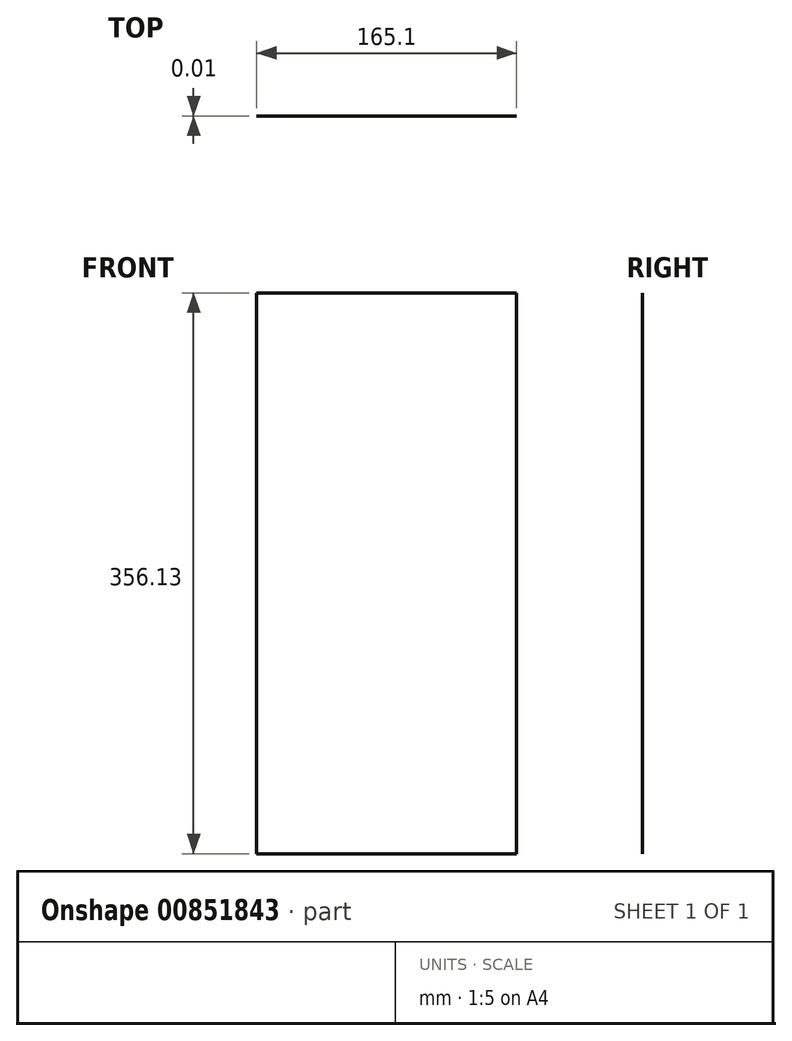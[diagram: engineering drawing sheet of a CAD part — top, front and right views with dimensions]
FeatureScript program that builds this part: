
annotation { "Feature Type Name" : "Feature", "Feature Type Description" : "" }
export const myFeature = defineFeature(function(context is Context, id is Id, definition is map)
    precondition{}
    {
        {
            var Q0;
            Q0=qCreatedBy(makeId("Front.planeOp"),FACE);
            var sketch = newSketch(context, id + "F0", { "sketchPlane" : qUnion([Q0])});
            skLineSegment(sketch, "E0.bottom", {"start": v(-96.95, 163.97) * mm, "end": v(68.15, 163.97) * mm});
            skLineSegment(sketch, "E0.top", {"start": v(-96.95, -192.16) * mm, "end": v(68.15, -192.16) * mm});
            skLineSegment(sketch, "E0.left", {"start": v(-96.95, 163.97) * mm, "end": v(-96.95, -192.16) * mm});
            skLineSegment(sketch, "E0.right", {"start": v(68.15, 163.97) * mm, "end": v(68.15, -192.16) * mm});
            skSolve(sketch);
        }
        {
            var Q0;
            Q0=makeQuery(id+"F0.imprint","IMPRINT",FACE,{"disambiguationData":[TD([[makeQuery(id+"F0.imprint","IMPRINT",EDGE,{"derivedFrom":sQuery(id+"F0.wireOp",EDGE,"E0.bottom")}),-1.0]])]});
            var Q1;
            Q1 = qSketchRegion(id + "F0", true);
            extrude(context, id + "F1", {"entities" : qUnion([Q0, Q1]), "depth" : 1 / 101.6 * mm, "offsetDistance" : 25.4 * mm});
        }
        {
            var Q0;
            Q0=makeQuery(id+"F1.opExtrude","SWEPT_FACE",FACE,{"disambiguationData":[OSD([sQuery(id+"F0.wireOp",EDGE,"E0.bottom")])]});
            var sketch = newSketch(context, id + "F2", { "sketchPlane" : qUnion([Q0])});
            skLineSegment(sketch, "E1", {"start": v(-14.4, -6.35) * mm, "end": v(-14.4, 0) * mm});
            skPoint(sketch, "E2", {"position": v(-14.4, -3.18) * mm});
            skSolve(sketch);
        }
        {
            var Q0;
            Q0=sQuery(id+"F2.wireOp",VERTEX,"E2");
            var Q1;
            Q1=makeQuery(id+"F1.opExtrude","SWEPT_BODY",BODY,{"disambiguationData":[OSD([sQuery(id+"F0.wireOp",EDGE,"E0.bottom"),sQuery(id+"F0.wireOp",EDGE,"E0.top"),sQuery(id+"F0.wireOp",EDGE,"E0.left"),sQuery(id+"F0.wireOp",EDGE,"E0.right")])]});
            hole(context, id + "F3", {"style" : HoleStyle.SIMPLE, "endStyle" : HoleEndStyle.BLIND, "standardTappedOrClearance" : lookupTablePath({ "standard" : "ANSI", "engagement" : "75%", "pitch" : "32 tpi", "size" : "#8", "type" : "Tapped" }), "standardBlindInLast" : lookupTablePath({ "standard" : "ANSI", "engagement" : "75%", "pitch" : "32 tpi", "size" : "#8", "type" : "Tapped" }), "holeDiameter" : 3.45 * mm, "majorDiameter" : 4.17 * mm, "showTappedDepth" : true, "holeDepth" : 18.26 * mm, "isTappedThrough" : true, "tappedDepth" : 15.88 * mm, "tapClearance" : 3, "locations" : qUnion([Q0]), "scope" : qUnion([Q1])});
        }
    });
